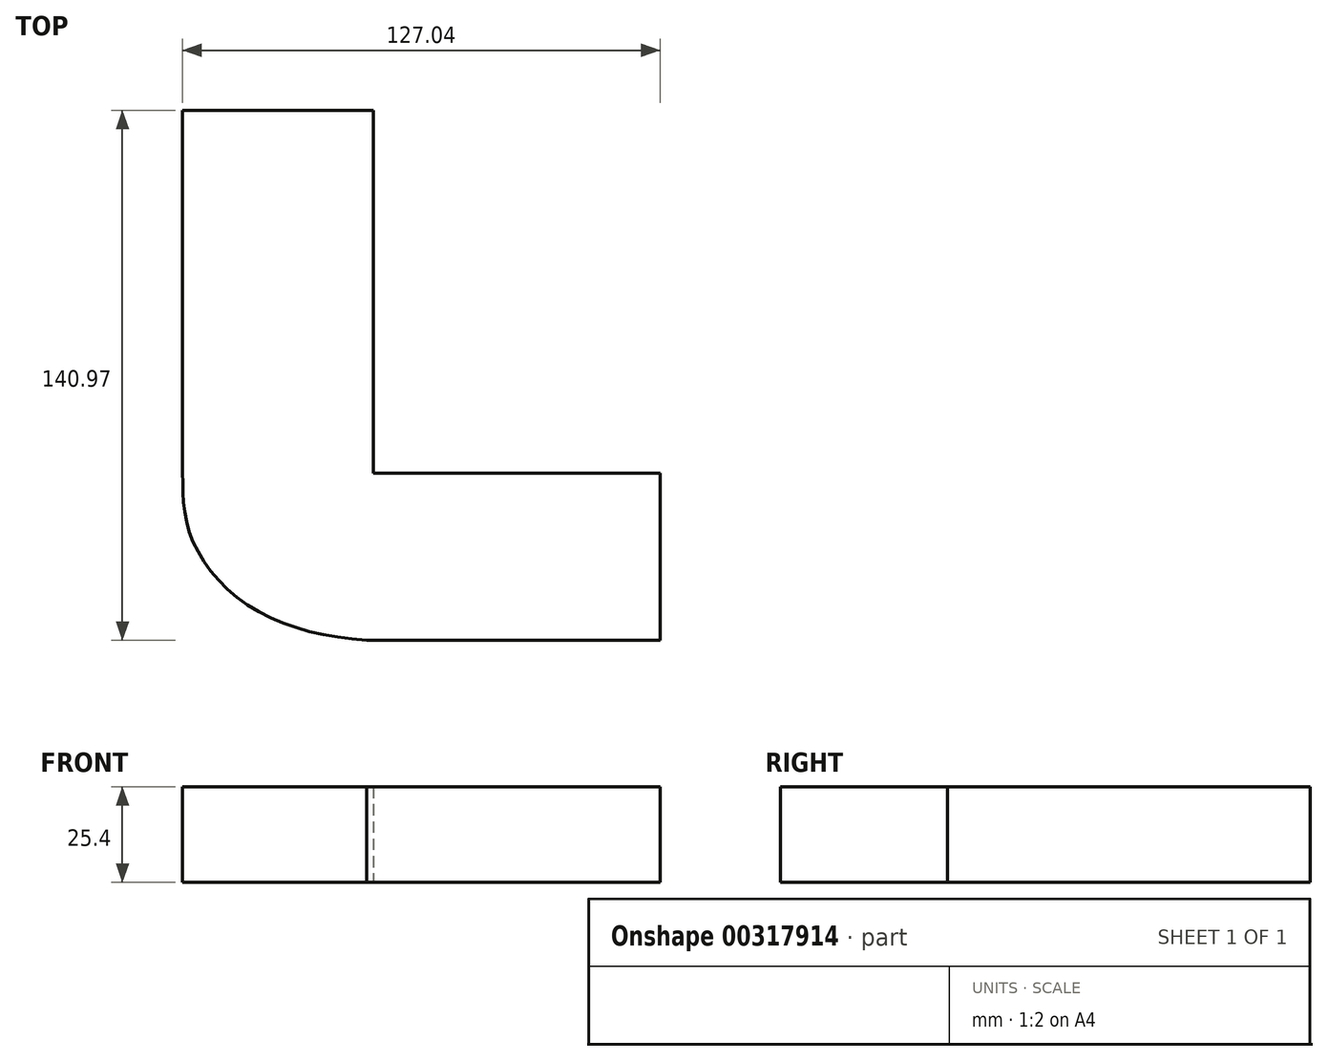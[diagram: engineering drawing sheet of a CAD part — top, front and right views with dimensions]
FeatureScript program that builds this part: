
annotation { "Feature Type Name" : "Feature", "Feature Type Description" : "" }
export const myFeature = defineFeature(function(context is Context, id is Id, definition is map)
    precondition{}
    {
        {
            var Q0;
            Q0=qCreatedBy(makeId("Top.planeOp"),FACE);
            var sketch = newSketch(context, id + "F0", { "sketchPlane" : qUnion([Q0])});
            skLineSegment(sketch, "E0.bottom", {"start": v(-37.31, 30.44) * mm, "end": v(13.49, 30.44) * mm});
            skLineSegment(sketch, "E0.top", {"start": v(-37.31, -66.08) * mm, "end": v(13.49, -66.08) * mm});
            skLineSegment(sketch, "E0.left", {"start": v(-37.31, 30.44) * mm, "end": v(-37.31, -66.08) * mm});
            skLineSegment(sketch, "E0.right", {"start": v(13.49, 30.44) * mm, "end": v(13.49, -66.08) * mm});
            skLineSegment(sketch, "E1.bottom", {"start": v(11.67, -66.08) * mm, "end": v(89.73, -66.08) * mm});
            skLineSegment(sketch, "E1.top", {"start": v(11.67, -110.53) * mm, "end": v(89.73, -110.53) * mm});
            skLineSegment(sketch, "E1.left", {"start": v(11.67, -66.08) * mm, "end": v(11.67, -110.53) * mm});
            skLineSegment(sketch, "E1.right", {"start": v(89.73, -66.08) * mm, "end": v(89.73, -110.53) * mm});
            skPoint(sketch, "E2.2.internal.snap0", {"position": v(11.67, -88.3) * mm});
            skFitSpline(sketch, "E3", {"points": [v(-37.31, -66.08) * mm, v(-35.15, -82.72) * mm, v(-19.96, -101.2) * mm, v(11.67, -110.53) * mm], "startDerivative": vector(0.5, -59.09) * mm, "endDerivative": vector(89.77, -5.84) * mm});
            skSolve(sketch);
        }
        {
            var Q0;
            Q0=makeQuery(id+"F0.imprint","IMPRINT",FACE,{"disambiguationData":[TD([[makeQuery(id+"F0.imprint","IMPRINT",EDGE,{"derivedFrom":sQuery(id+"F0.wireOp",EDGE,"E0.bottom")}),-1.0]])]});
            var Q1;
            Q1=makeQuery(id+"F0.imprint","IMPRINT",FACE,{"disambiguationData":[TD([[makeQuery(id+"F0.imprint","IMPRINT",EDGE,{"derivedFrom":sQuery(id+"F0.wireOp",EDGE,"E0.top")}),-1.0]])]});
            var Q2;
            Q2=makeQuery(id+"F0.imprint","IMPRINT",FACE,{"disambiguationData":[TD([[makeQuery(id+"F0.imprint","IMPRINT",EDGE,{"derivedFrom":sQuery(id+"F0.wireOp",EDGE,"E1.top")}),1.0]])]});
            extrude(context, id + "F1", {"entities" : qUnion([Q0, Q1, Q2]), "depth" : 25.4 * mm});
        }
    });
